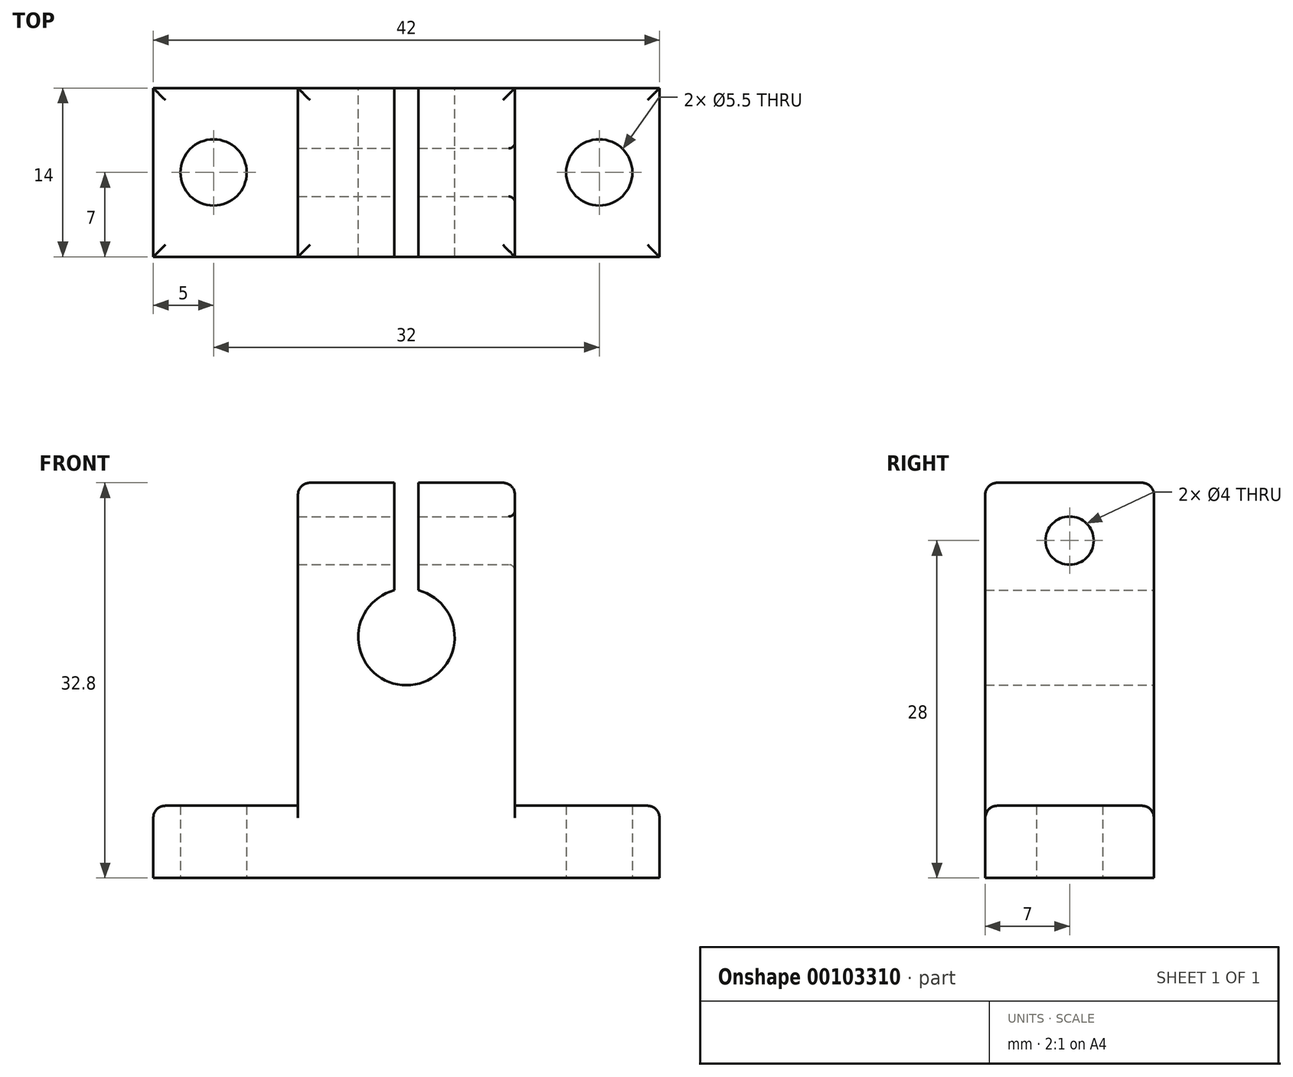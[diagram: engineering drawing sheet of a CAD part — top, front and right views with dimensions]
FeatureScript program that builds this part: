
annotation { "Feature Type Name" : "Feature", "Feature Type Description" : "" }
export const myFeature = defineFeature(function(context is Context, id is Id, definition is map)
    precondition{}
    {
        {
            var Q0;
            Q0=qCreatedBy(makeId("Front.planeOp"),FACE);
            var sketch = newSketch(context, id + "F0", { "sketchPlane" : qUnion([Q0])});
            skLineSegment(sketch, "E0.bottom", {"start": v(-21, 6) * mm, "end": v(-9, 6) * mm});
            skLineSegment(sketch, "E0.top", {"start": v(-21, 0) * mm, "end": v(21, 0) * mm});
            skLineSegment(sketch, "E0.left", {"start": v(-21, 6) * mm, "end": v(-21, 0) * mm});
            skLineSegment(sketch, "E0.right", {"start": v(21, 6) * mm, "end": v(21, 0) * mm});
            skLineSegment(sketch, "E1.bottom", {"start": v(-9, 32.8) * mm, "end": v(-1, 32.8) * mm});
            skLineSegment(sketch, "E1.left", {"start": v(-9, 32.8) * mm, "end": v(-9, 6) * mm});
            skLineSegment(sketch, "E1.right", {"start": v(9, 32.8) * mm, "end": v(9, 6) * mm});
            skPoint(sketch, "E2", {"position": v(-9, 6) * mm});
            skPoint(sketch, "E3", {"position": v(9, 6) * mm});
            skLineSegment(sketch, "E4.trimOffspring", {"start": v(9, 6) * mm, "end": v(21, 6) * mm});
            skLineSegment(sketch, "E5", {"start": v(-26.53, 20) * mm, "end": v(25.47, 20) * mm, "construction": true});
            skLineSegment(sketch, "E6", {"start": v(0, 47.77) * mm, "end": v(0, -24.77) * mm, "construction": true});
            skPoint(sketch, "E7", {"position": v(0, 20) * mm});
            skArc(sketch, "E8", {"start": v(-1, 23.87) * mm, "mid": v(0, 16) * mm, "end": v(1, 23.87) * mm});
            skLineSegment(sketch, "E9", {"start": v(-1, 32.8) * mm, "end": v(-1, 23.87) * mm});
            skLineSegment(sketch, "E10", {"start": v(1, 32.8) * mm, "end": v(1, 23.87) * mm});
            skLineSegment(sketch, "E11.trimOffspring", {"start": v(1, 32.8) * mm, "end": v(9, 32.8) * mm});
            skSolve(sketch);
        }
        {
            var Q0;
            Q0=makeQuery(id+"F0.imprint","IMPRINT",FACE,{"disambiguationData":[TD([[makeQuery(id+"F0.imprint","IMPRINT",EDGE,{"derivedFrom":sQuery(id+"F0.wireOp",EDGE,"E0.bottom")}),-1.0]])]});
            extrude(context, id + "F1", {"entities" : qUnion([Q0]), "depth" : 14 * mm});
        }
        {
            var Q0;
            Q0=qCreatedBy(makeId("Top.planeOp"),FACE);
            var sketch = newSketch(context, id + "F2", { "sketchPlane" : qUnion([Q0])});
            skLineSegment(sketch, "E12", {"start": v(-26.72, -7) * mm, "end": v(28.4, -7) * mm, "construction": true});
            skLineSegment(sketch, "E13", {"start": v(-16, 7.27) * mm, "end": v(-16, -22.73) * mm, "construction": true});
            skLineSegment(sketch, "E14", {"start": v(16, 4.5) * mm, "end": v(16, -25.5) * mm, "construction": true});
            skPoint(sketch, "E15", {"position": v(-16, -7) * mm});
            skPoint(sketch, "E16", {"position": v(16, -7) * mm});
            skCircle(sketch, "E17", {"center": v(-16, -7) * mm, "radius": 2.75 * mm});
            skCircle(sketch, "E18", {"center": v(16, -7) * mm, "radius": 2.75 * mm});
            skSolve(sketch);
        }
        {
            var Q0;
            Q0=makeQuery(id+"F2.imprint","IMPRINT",FACE,{"disambiguationData":[TD([[makeQuery(id+"F2.imprint","IMPRINT",EDGE,{"derivedFrom":sQuery(id+"F2.wireOp",EDGE,"E18")}),1.0]])]});
            var Q1;
            Q1=makeQuery(id+"F2.imprint","IMPRINT",FACE,{"disambiguationData":[TD([[makeQuery(id+"F2.imprint","IMPRINT",EDGE,{"derivedFrom":sQuery(id+"F2.wireOp",EDGE,"E17")}),1.0]])]});
            extrude(context, id + "F3", {"entities" : qUnion([Q0, Q1]), "operationType" : NewBodyOperationType.REMOVE, "depth" : 6 * mm});
        }
        {
            var Q0;
            Q0=makeQuery(id+"F1.opExtrude","SWEPT_EDGE",EDGE,{"disambiguationData":[OSD([sQuery(id+"F0.wireOp",EDGE,"E0.bottom"),sQuery(id+"F0.wireOp",EDGE,"E0.left")])]});
            var Q1;
            Q1=makeQuery(id+"F1.opExtrude","CAP_EDGE",EDGE,{"disambiguationData":[OSD([sQuery(id+"F0.wireOp",EDGE,"E0.bottom")])],"isStart":true});
            var Q2;
            Q2=makeQuery(id+"F1.opExtrude","CAP_EDGE",EDGE,{"disambiguationData":[OSD([sQuery(id+"F0.wireOp",EDGE,"E0.bottom")])],"isStart":false});
            var Q3;
            Q3=makeQuery(id+"F1.opExtrude","CAP_EDGE",EDGE,{"disambiguationData":[OSD([sQuery(id+"F0.wireOp",EDGE,"E4.trimOffspring")])],"isStart":false});
            var Q4;
            Q4=makeQuery(id+"F1.opExtrude","SWEPT_EDGE",EDGE,{"disambiguationData":[OSD([sQuery(id+"F0.wireOp",EDGE,"E0.right"),sQuery(id+"F0.wireOp",EDGE,"E4.trimOffspring")])]});
            var Q5;
            Q5=makeQuery(id+"F1.opExtrude","CAP_EDGE",EDGE,{"disambiguationData":[OSD([sQuery(id+"F0.wireOp",EDGE,"E4.trimOffspring")])],"isStart":true});
            var Q6;
            Q6=makeQuery(id+"F1.opExtrude","SWEPT_EDGE",EDGE,{"disambiguationData":[OSD([sQuery(id+"F0.wireOp",EDGE,"E1.bottom"),sQuery(id+"F0.wireOp",EDGE,"E1.left")])]});
            var Q7;
            Q7=makeQuery(id+"F1.opExtrude","SWEPT_EDGE",EDGE,{"disambiguationData":[OSD([sQuery(id+"F0.wireOp",EDGE,"E1.right"),sQuery(id+"F0.wireOp",EDGE,"E11.trimOffspring")])]});
            var Q8;
            Q8=makeQuery(id+"F1.opExtrude","CAP_EDGE",EDGE,{"disambiguationData":[OSD([sQuery(id+"F0.wireOp",EDGE,"E11.trimOffspring")])],"isStart":true});
            var Q9;
            Q9=makeQuery(id+"F1.opExtrude","CAP_EDGE",EDGE,{"disambiguationData":[OSD([sQuery(id+"F0.wireOp",EDGE,"E1.bottom")])],"isStart":true});
            var Q10;
            Q10=makeQuery(id+"F1.opExtrude","CAP_EDGE",EDGE,{"disambiguationData":[OSD([sQuery(id+"F0.wireOp",EDGE,"E1.bottom")])],"isStart":false});
            var Q11;
            Q11=makeQuery(id+"F1.opExtrude","CAP_EDGE",EDGE,{"disambiguationData":[OSD([sQuery(id+"F0.wireOp",EDGE,"E11.trimOffspring")])],"isStart":false});
            fillet(context, id + "F4", {"entities" : qUnion([Q0, Q1, Q2, Q3, Q4, Q5, Q6, Q7, Q8, Q9, Q10, Q11]), "radius" : 1 * mm, "tangentPropagation" : true, "allowEdgeOverflow" : false});
        }
        {
            var Q0;
            Q0=qCreatedBy(makeId("Right.planeOp"),FACE);
            var sketch = newSketch(context, id + "F5", { "sketchPlane" : qUnion([Q0])});
            skLineSegment(sketch, "E19", {"start": v(-7, 40.06) * mm, "end": v(-7, -6.67) * mm, "construction": true});
            skLineSegment(sketch, "E20", {"start": v(-18.45, 28) * mm, "end": v(2.78, 28) * mm, "construction": true});
            skCircle(sketch, "E21", {"center": v(-7, 28) * mm, "radius": 2 * mm});
            skSolve(sketch);
        }
        {
            var Q0;
            Q0 = qSketchRegion(id + "F5", true);
            var Q1;
            Q1=sQuery(id+"F5.wireOp",EDGE,"E21");
            extrude(context, id + "F6", {"entities" : qUnion([Q0]), "operationType" : NewBodyOperationType.REMOVE, "surfaceEntities" : qUnion([Q1]), "oppositeDirection" : true, "depth" : 10 * mm, "hasSecondDirection" : true, "secondDirectionOppositeDirection" : false, "secondDirectionDepth" : 9 * mm});
        }
        {
            var Q0;
            Q0=makeQuery(id+"F6.boolean.opBoolean","INTERSECT",EDGE,{"derivedFrom":[makeQuery(id+"F1.opExtrude","SWEPT_FACE",FACE,{"disambiguationData":[OSD([sQuery(id+"F0.wireOp",EDGE,"E1.right")])]}),makeQuery(id+"F6.opExtrude","SWEPT_FACE",FACE,{"disambiguationData":[OSD([sQuery(id+"F5.wireOp",EDGE,"E21")])]})]});
            fillet(context, id + "F7", {"entities" : qUnion([Q0]), "radius" : .5 * mm, "tangentPropagation" : true, "allowEdgeOverflow" : false});
        }
    });
